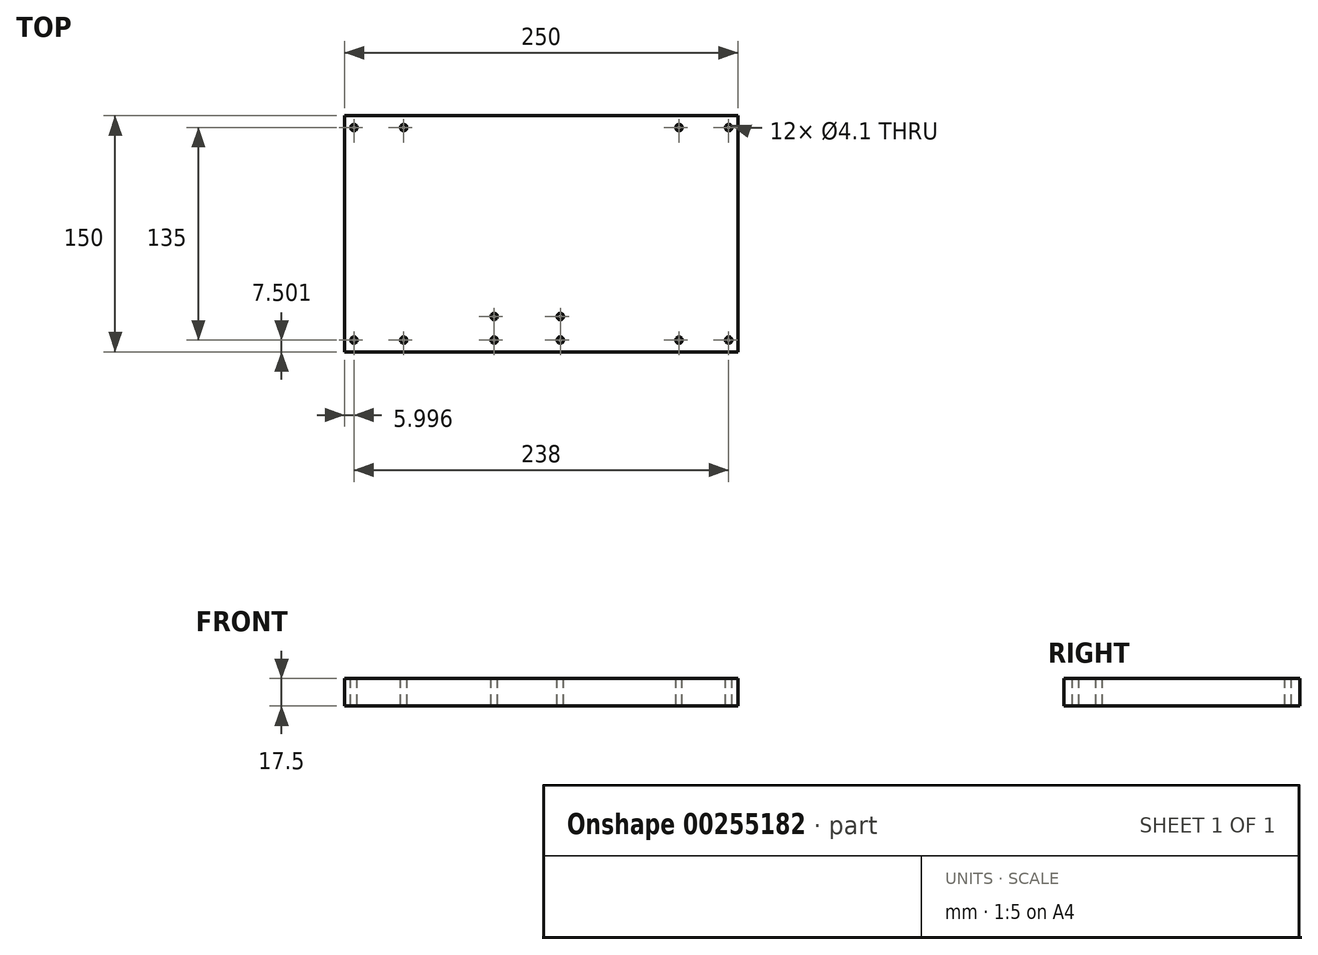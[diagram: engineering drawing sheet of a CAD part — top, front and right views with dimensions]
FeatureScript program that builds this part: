
annotation { "Feature Type Name" : "Feature", "Feature Type Description" : "" }
export const myFeature = defineFeature(function(context is Context, id is Id, definition is map)
    precondition{}
    {
        {
            var Q0;
            Q0=qCreatedBy(makeId("Top.planeOp"),FACE);
            var sketch = newSketch(context, id + "F0", { "sketchPlane" : qUnion([Q0])});
            skLineSegment(sketch, "E0.bottom", {"start": v(-79.94, 107.56) * mm, "end": v(170.06, 107.56) * mm});
            skLineSegment(sketch, "E0.top", {"start": v(-79.94, -42.44) * mm, "end": v(170.06, -42.44) * mm});
            skLineSegment(sketch, "E0.left", {"start": v(-79.94, 107.56) * mm, "end": v(-79.94, -42.44) * mm});
            skLineSegment(sketch, "E0.right", {"start": v(170.06, 107.56) * mm, "end": v(170.06, -42.44) * mm});
            skSolve(sketch);
        }
        {
            var Q0;
            Q0 = qSketchRegion(id + "F0", true);
            extrude(context, id + "F1", {"entities" : qUnion([Q0]), "depth" : 17.5 * mm});
        }
        {
            var Q0;
            Q0=makeQuery(id+"F1.opExtrude","CAP_FACE",FACE,{"disambiguationData":[OSD([sQuery(id+"F0.wireOp",EDGE,"E0.bottom"),sQuery(id+"F0.wireOp",EDGE,"E0.top"),sQuery(id+"F0.wireOp",EDGE,"E0.left"),sQuery(id+"F0.wireOp",EDGE,"E0.right")])],"isStart":false});
            var sketch = newSketch(context, id + "F2", { "sketchPlane" : qUnion([Q0])});
            skLineSegment(sketch, "E1", {"start": v(-79.94, -34.94) * mm, "end": v(9.1, -34.94) * mm, "construction": true});
            skLineSegment(sketch, "E2", {"start": v(9.1, -34.94) * mm, "end": v(15.1, -34.94) * mm, "construction": true});
            skLineSegment(sketch, "E3", {"start": v(15.1, -34.94) * mm, "end": v(57.1, -34.94) * mm, "construction": true});
            skLineSegment(sketch, "E4", {"start": v(57.1, -34.94) * mm, "end": v(57.1, -19.94) * mm, "construction": true});
            skLineSegment(sketch, "E5", {"start": v(57.1, -19.94) * mm, "end": v(15.1, -19.94) * mm, "construction": true});
            skPoint(sketch, "E6", {"position": v(-73.94, -34.94) * mm});
            skPoint(sketch, "E7", {"position": v(-42.37, -34.94) * mm});
            skLineSegment(sketch, "E8", {"start": v(170.06, -34.94) * mm, "end": v(164.06, -34.94) * mm, "construction": true});
            skLineSegment(sketch, "E9", {"start": v(164.06, -34.94) * mm, "end": v(132.49, -34.94) * mm, "construction": true});
            skLineSegment(sketch, "E10", {"start": v(-79.94, 32.56) * mm, "end": v(170.06, 32.56) * mm, "construction": true});
            skPoint(sketch, "E11.MirrorP", {"position": v(-73.94, 100.06) * mm});
            skPoint(sketch, "E12.MirrorP", {"position": v(-42.37, 100.06) * mm});
            skLineSegment(sketch, "E13.MirrorCS", {"start": v(164.06, 100.06) * mm, "end": v(132.49, 100.06) * mm, "construction": true});
            skLineSegment(sketch, "E14", {"start": v(-73.94, -34.94) * mm, "end": v(-42.37, -34.94) * mm, "construction": true});
            skSolve(sketch);
        }
        {
            var Q0;
            Q0=sQuery(id+"F2.wireOp",VERTEX,"E11.MirrorP");
            var Q1;
            Q1=sQuery(id+"F2.wireOp",VERTEX,"E12.MirrorP");
            var Q2;
            Q2=sQuery(id+"F2.wireOp",VERTEX,"E13.MirrorCS.end");
            var Q3;
            Q3=sQuery(id+"F2.wireOp",VERTEX,"E13.MirrorCS.start");
            var Q4;
            Q4=sQuery(id+"F2.wireOp",VERTEX,"E9.start");
            var Q5;
            Q5=sQuery(id+"F2.wireOp",VERTEX,"E9.end");
            var Q6;
            Q6=sQuery(id+"F2.wireOp",VERTEX,"E5.start");
            var Q7;
            Q7=sQuery(id+"F2.wireOp",VERTEX,"E4.start");
            var Q8;
            Q8=sQuery(id+"F2.wireOp",VERTEX,"E5.end");
            var Q9;
            Q9=sQuery(id+"F2.wireOp",VERTEX,"E3.start");
            var Q10;
            Q10=sQuery(id+"F2.wireOp",VERTEX,"E7");
            var Q11;
            Q11=sQuery(id+"F2.wireOp",VERTEX,"E6");
            var Q12;
            Q12=makeQuery(id+"F1.opExtrude","SWEPT_BODY",BODY,{"disambiguationData":[OSD([sQuery(id+"F0.wireOp",EDGE,"E0.bottom"),sQuery(id+"F0.wireOp",EDGE,"E0.top"),sQuery(id+"F0.wireOp",EDGE,"E0.left"),sQuery(id+"F0.wireOp",EDGE,"E0.right")])]});
            hole(context, id + "F3", {"style" : HoleStyle.SIMPLE, "endStyle" : HoleEndStyle.THROUGH, "holeDiameter" : 4.1 * mm, "tappedDepth" : 12 * mm, "tapClearance" : 3, "locations" : qUnion([Q0, Q1, Q2, Q3, Q4, Q5, Q6, Q7, Q8, Q9, Q10, Q11]), "scope" : qUnion([Q12])});
        }
        {
            var Q0;
            Q0=makeQuery(id+"F1.opExtrude","CAP_FACE",FACE,{"disambiguationData":[OSD([sQuery(id+"F0.wireOp",EDGE,"E0.bottom"),sQuery(id+"F0.wireOp",EDGE,"E0.top"),sQuery(id+"F0.wireOp",EDGE,"E0.left"),sQuery(id+"F0.wireOp",EDGE,"E0.right")])],"isStart":false});
            var sketch = newSketch(context, id + "F4", { "sketchPlane" : qUnion([Q0])});
            skLineSegment(sketch, "E15", {"start": v(45.06, 107.56) * mm, "end": v(45.06, 70.06) * mm});
            skPoint(sketch, "E15.endSnap0", {"position": v(45.06, -42.44) * mm});
            skLineSegment(sketch, "E16", {"start": v(45.06, 70.06) * mm, "end": v(35.06, 70.06) * mm});
            skLineSegment(sketch, "E17", {"start": v(35.06, 70.06) * mm, "end": v(35.06, 32.56) * mm});
            skLineSegment(sketch, "E18", {"start": v(35.06, 32.56) * mm, "end": v(45.06, 32.56) * mm});
            skLineSegment(sketch, "E19", {"start": v(45.06, 32.56) * mm, "end": v(45.06, -4.94) * mm});
            skLineSegment(sketch, "E20", {"start": v(45.06, -4.94) * mm, "end": v(35.06, -4.94) * mm});
            skLineSegment(sketch, "E21", {"start": v(35.06, -4.94) * mm, "end": v(35.06, -42.44) * mm});
            skSolve(sketch);
        }
        {
            var Q0;
            Q0 = qSketchRegion(id + "F4", true);
            var Q1;
            Q1=sQuery(id+"F4.wireOp",EDGE,"E15");
            var Q2;
            Q2=sQuery(id+"F4.wireOp",EDGE,"E16");
            var Q3;
            Q3=sQuery(id+"F4.wireOp",EDGE,"E17");
            var Q4;
            Q4=sQuery(id+"F4.wireOp",EDGE,"E18");
            var Q5;
            Q5=sQuery(id+"F4.wireOp",EDGE,"E19");
            var Q6;
            Q6=sQuery(id+"F4.wireOp",EDGE,"E20");
            var Q7;
            Q7=sQuery(id+"F4.wireOp",EDGE,"E21");
            extrude(context, id + "F5", {"entities" : qUnion([Q0]), "bodyType" : ToolBodyType.SURFACE, "surfaceEntities" : qUnion([Q1, Q2, Q3, Q4, Q5, Q6, Q7]), "oppositeDirection" : true, "depth" : 40 * mm});
        }
    });
